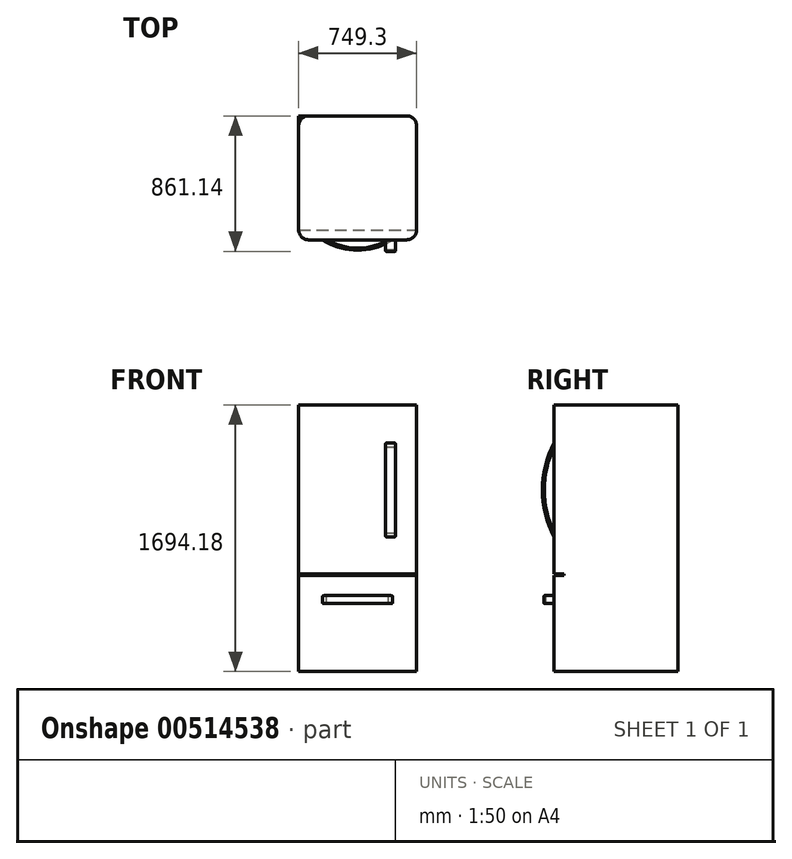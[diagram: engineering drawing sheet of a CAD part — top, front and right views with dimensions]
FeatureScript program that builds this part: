
annotation { "Feature Type Name" : "Feature", "Feature Type Description" : "" }
export const myFeature = defineFeature(function(context is Context, id is Id, definition is map)
    precondition{}
    {
        {
            var Q0;
            Q0=qCreatedBy(makeId("Top.planeOp"),FACE);
            var sketch = newSketch(context, id + "F0", { "sketchPlane" : qUnion([Q0])});
            skLineSegment(sketch, "E0.bottom", {"start": v(374.65, 393.7) * mm, "end": v(-374.65, 393.7) * mm});
            skLineSegment(sketch, "E0.top", {"start": v(374.65, -393.7) * mm, "end": v(-374.65, -393.7) * mm});
            skLineSegment(sketch, "E0.left", {"start": v(374.65, 393.7) * mm, "end": v(374.65, -393.7) * mm});
            skLineSegment(sketch, "E0.right", {"start": v(-374.65, 393.7) * mm, "end": v(-374.65, -393.7) * mm});
            skPoint(sketch, "E0.middle", {"position": v(0, 0) * mm});
            skSolve(sketch);
        }
        {
            var Q0;
            Q0=makeQuery(id+"F0.imprint","IMPRINT",FACE,{"disambiguationData":[TD([[makeQuery(id+"F0.imprint","IMPRINT",EDGE,{"derivedFrom":sQuery(id+"F0.wireOp",EDGE,"E0.bottom")}),1.0]])]});
            extrude(context, id + "F1", {"entities" : qUnion([Q0]), "depth" : 1694.18 * mm, "offsetDistance" : 25.4 * mm});
        }
        {
            var Q0;
            Q0=makeQuery(id+"F1.opExtrude","SWEPT_FACE",FACE,{"disambiguationData":[OSD([sQuery(id+"F0.wireOp",EDGE,"E0.top")])]});
            var sketch = newSketch(context, id + "F2", { "sketchPlane" : qUnion([Q0])});
            skLineSegment(sketch, "E1.bottom", {"start": v(-374.65, 1694.18) * mm, "end": v(374.65, 1694.18) * mm});
            skLineSegment(sketch, "E1.top", {"start": v(-374.65, 619.76) * mm, "end": v(374.65, 619.76) * mm});
            skLineSegment(sketch, "E1.left", {"start": v(-374.65, 1694.18) * mm, "end": v(-374.65, 619.76) * mm});
            skLineSegment(sketch, "E1.right", {"start": v(374.65, 1694.18) * mm, "end": v(374.65, 619.76) * mm});
            skLineSegment(sketch, "E2.bottom", {"start": v(374.65, 0) * mm, "end": v(-374.65, 0) * mm});
            skLineSegment(sketch, "E2.top", {"start": v(374.65, 609.6) * mm, "end": v(-374.65, 609.6) * mm});
            skLineSegment(sketch, "E2.left", {"start": v(374.65, 0) * mm, "end": v(374.65, 609.6) * mm});
            skLineSegment(sketch, "E2.right", {"start": v(-374.65, 0) * mm, "end": v(-374.65, 609.6) * mm});
            skSolve(sketch);
        }
        {
            var Q0;
            {var subQ0=sQuery(id+"F2.wireOp",EDGE,"E1.top");Q0=makeQuery(id+"F2.imprint","IMPRINT",FACE,{"disambiguationData":[TD([[makeQuery(id+"F2.imprint","IMPRINT",EDGE,{"derivedFrom":subQ0}),-1.0]])]});}
            extrude(context, id + "F3", {"entities" : qUnion([Q0]), "operationType" : NewBodyOperationType.REMOVE, "oppositeDirection" : true, "depth" : 63.5 * mm, "offsetDistance" : 25.4 * mm});
        }
        {
            var Q0;
            {var subQ0=sQuery(id+"F0.wireOp",EDGE,"E0.left");var subQ1=sQuery(id+"F0.wireOp",EDGE,"E0.top");Q0=makeQuery(id+"F3.boolean.opBoolean","SPLIT",EDGE,{"disambiguationData":[TD([makeQuery(id+"F3.opExtrude","SWEPT_FACE",FACE,{"disambiguationData":[OSD([sQuery(id+"F2.wireOp",EDGE,"E1.top")])]})])],"derivedFrom":makeQuery(id+"F1.opExtrude","SWEPT_EDGE",EDGE,{"disambiguationData":[OSD([subQ1,subQ0])]})});}
            var Q1;
            {var subQ0=sQuery(id+"F0.wireOp",EDGE,"E0.left");var subQ1=sQuery(id+"F0.wireOp",EDGE,"E0.top");Q1=makeQuery(id+"F3.boolean.opBoolean","SPLIT",EDGE,{"disambiguationData":[TD([makeQuery(id+"F3.opExtrude","SWEPT_FACE",FACE,{"disambiguationData":[OSD([sQuery(id+"F2.wireOp",EDGE,"E2.top")])]})])],"derivedFrom":makeQuery(id+"F1.opExtrude","SWEPT_EDGE",EDGE,{"disambiguationData":[OSD([subQ1,subQ0])]})});}
            var Q2;
            {var subQ0=sQuery(id+"F0.wireOp",EDGE,"E0.right");var subQ1=sQuery(id+"F0.wireOp",EDGE,"E0.top");Q2=makeQuery(id+"F3.boolean.opBoolean","SPLIT",EDGE,{"disambiguationData":[TD([makeQuery(id+"F3.opExtrude","SWEPT_FACE",FACE,{"disambiguationData":[OSD([sQuery(id+"F2.wireOp",EDGE,"E1.top")])]})])],"derivedFrom":makeQuery(id+"F1.opExtrude","SWEPT_EDGE",EDGE,{"disambiguationData":[OSD([subQ1,subQ0])]})});}
            var Q3;
            {var subQ0=sQuery(id+"F0.wireOp",EDGE,"E0.right");var subQ1=sQuery(id+"F0.wireOp",EDGE,"E0.top");Q3=makeQuery(id+"F3.boolean.opBoolean","SPLIT",EDGE,{"disambiguationData":[TD([makeQuery(id+"F3.opExtrude","SWEPT_FACE",FACE,{"disambiguationData":[OSD([sQuery(id+"F2.wireOp",EDGE,"E2.top")])]})])],"derivedFrom":makeQuery(id+"F1.opExtrude","SWEPT_EDGE",EDGE,{"disambiguationData":[OSD([subQ1,subQ0])]})});}
            var Q4;
            Q4=makeQuery(id+"F1.opExtrude","SWEPT_EDGE",EDGE,{"disambiguationData":[OSD([sQuery(id+"F0.wireOp",EDGE,"E0.bottom"),sQuery(id+"F0.wireOp",EDGE,"E0.left")])]});
            var Q5;
            Q5=makeQuery(id+"F1.opExtrude","SWEPT_EDGE",EDGE,{"disambiguationData":[OSD([sQuery(id+"F0.wireOp",EDGE,"E0.bottom"),sQuery(id+"F0.wireOp",EDGE,"E0.right")])]});
            fillet(context, id + "F4", {"entities" : qUnion([Q0, Q1, Q2, Q3, Q4, Q5]), "radius" : 63.5 * mm, "tangentPropagation" : true, "allowEdgeOverflow" : false});
        }
        {
            var Q0;
            Q0=makeQuery(id+"F1.opExtrude","CAP_FACE",FACE,{"disambiguationData":[OSD([sQuery(id+"F0.wireOp",EDGE,"E0.bottom"),sQuery(id+"F0.wireOp",EDGE,"E0.top"),sQuery(id+"F0.wireOp",EDGE,"E0.left"),sQuery(id+"F0.wireOp",EDGE,"E0.right")])],"isStart":true});
            cPlane(context, id + "F5", {"entities" : qUnion([Q0]), "cplaneType" : CPlaneType.OFFSET, "offset" : 457.2 * mm, "oppositeDirection" : true, "width" : 152.4 * mm, "height" : 152.4 * mm});
        }
        {
            var Q0;
            Q0=qCreatedBy(id+"F5.planeOp",FACE);
            var sketch = newSketch(context, id + "F6", { "sketchPlane" : qUnion([Q0])});
            skLineSegment(sketch, "E3", {"start": v(-311.15, 477.49) * mm, "end": v(-209.55, 477.49) * mm});
            skLineSegment(sketch, "E4", {"start": v(-209.55, 477.49) * mm, "end": v(209.55, 477.49) * mm});
            skLineSegment(sketch, "E5", {"start": v(209.55, 477.49) * mm, "end": v(311.15, 477.49) * mm});
            skLineSegment(sketch, "E6", {"start": v(0, 0) * mm, "end": v(0, 4953.26) * mm});
            skLineSegment(sketch, "E7", {"start": v(-209.55, 477.49) * mm, "end": v(0, 477.49) * mm});
            skCircle(sketch, "E8", {"center": v(0, 50.8) * mm, "radius": 254 * mm});
            skArc(sketch, "E9", {"start": v(209.67, 194.17) * mm, "mid": v(5.68, 304.74) * mm, "end": v(-203.05, 203.4) * mm});
            skSolve(sketch);
        }
        {
            var Q0;
            Q0=makeQuery(id+"F2.imprint","IMPRINT",FACE,{"disambiguationData":[TD([[makeQuery(id+"F2.imprint","IMPRINT",EDGE,{"derivedFrom":sQuery(id+"F2.wireOp",EDGE,"E2.bottom")}),-1.0]])]});
            var sketch = newSketch(context, id + "F7", { "sketchPlane" : qUnion([Q0])});
            skLineSegment(sketch, "E10", {"start": v(-209.55, 609.6) * mm, "end": v(-209.55, 457.2) * mm});
            skLineSegment(sketch, "E11", {"start": v(-311.15, 457.2) * mm, "end": v(-209.55, 457.2) * mm});
            skLineSegment(sketch, "E12", {"start": v(-209.55, 457.2) * mm, "end": v(209.55, 457.2) * mm});
            skLineSegment(sketch, "E13", {"start": v(209.55, 457.2) * mm, "end": v(311.15, 457.2) * mm});
            skLineSegment(sketch, "E14.bottom", {"start": v(-196.85, 482.6) * mm, "end": v(-222.25, 482.6) * mm});
            skLineSegment(sketch, "E14.top", {"start": v(-196.85, 431.8) * mm, "end": v(-222.25, 431.8) * mm});
            skLineSegment(sketch, "E14.left", {"start": v(-196.85, 482.6) * mm, "end": v(-196.85, 431.8) * mm});
            skLineSegment(sketch, "E14.right", {"start": v(-222.25, 482.6) * mm, "end": v(-222.25, 431.8) * mm});
            skPoint(sketch, "E14.middle", {"position": v(-209.55, 457.2) * mm});
            skSolve(sketch);
        }
        {
            var Q0;
            Q0 = qSketchRegion(id + "F7", true);
            var Q1;
            Q1=sQuery(id+"F6.wireOp",EDGE,"E9");
            sweep(context, id + "F8", {"operationType" : NewBodyOperationType.ADD, "profiles" : qUnion([Q0]), "path" : qUnion([Q1])});
        }
        {
            var Q0;
            Q0=makeQuery(id+"F8.opSweep","SWEPT_EDGE",EDGE,{"disambiguationData":[OSD([sQuery(id+"F6.wireOp",EDGE,"E9"),sQuery(id+"F7.wireOp",EDGE,"E14.bottom"),sQuery(id+"F7.wireOp",EDGE,"E14.right")])]});
            var Q1;
            Q1=makeQuery(id+"F8.opSweep","SWEPT_EDGE",EDGE,{"disambiguationData":[OSD([sQuery(id+"F6.wireOp",EDGE,"E9"),sQuery(id+"F7.wireOp",EDGE,"E14.bottom"),sQuery(id+"F7.wireOp",EDGE,"E14.left")])]});
            var Q2;
            Q2=makeQuery(id+"F8.opSweep","SWEPT_EDGE",EDGE,{"disambiguationData":[OSD([sQuery(id+"F6.wireOp",EDGE,"E9"),sQuery(id+"F7.wireOp",EDGE,"E14.top"),sQuery(id+"F7.wireOp",EDGE,"E14.right")])]});
            var Q3;
            Q3=makeQuery(id+"F8.opSweep","SWEPT_EDGE",EDGE,{"disambiguationData":[OSD([sQuery(id+"F6.wireOp",EDGE,"E9"),sQuery(id+"F7.wireOp",EDGE,"E14.top"),sQuery(id+"F7.wireOp",EDGE,"E14.left")])]});
            fillet(context, id + "F9", {"entities" : qUnion([Q0, Q1, Q2, Q3]), "radius" : 5.08 * mm, "tangentPropagation" : true, "allowEdgeOverflow" : false});
        }
        {
            var Q0;
            Q0=makeQuery(id+"F2.imprint","IMPRINT",FACE,{"disambiguationData":[TD([[makeQuery(id+"F2.imprint","IMPRINT",EDGE,{"derivedFrom":sQuery(id+"F2.wireOp",EDGE,"E1.bottom")}),1.0]])]});
            var sketch = newSketch(context, id + "F10", { "sketchPlane" : qUnion([Q0])});
            skLineSegment(sketch, "E15", {"start": v(209.55, 1694.18) * mm, "end": v(209.55, 619.76) * mm});
            skLineSegment(sketch, "E16", {"start": v(209.55, 619.76) * mm, "end": v(209.55, 873.76) * mm});
            skLineSegment(sketch, "E17", {"start": v(209.55, 873.76) * mm, "end": v(209.55, 1440.18) * mm});
            skLineSegment(sketch, "E18", {"start": v(209.55, 1440.18) * mm, "end": v(209.55, 1694.18) * mm});
            skLineSegment(sketch, "E19.bottom", {"start": v(241.3, 1452.88) * mm, "end": v(177.8, 1452.88) * mm});
            skLineSegment(sketch, "E19.top", {"start": v(241.3, 1427.48) * mm, "end": v(177.8, 1427.48) * mm});
            skLineSegment(sketch, "E19.left", {"start": v(241.3, 1452.88) * mm, "end": v(241.3, 1427.48) * mm});
            skLineSegment(sketch, "E19.right", {"start": v(177.8, 1452.88) * mm, "end": v(177.8, 1427.48) * mm});
            skPoint(sketch, "E19.middle", {"position": v(209.55, 1440.18) * mm});
            skSolve(sketch);
        }
        {
            var Q0;
            Q0=makeQuery(id+"F1.opExtrude","SWEPT_FACE",FACE,{"disambiguationData":[OSD([sQuery(id+"F0.wireOp",EDGE,"E0.left")])]});
            cPlane(context, id + "F11", {"entities" : qUnion([Q0]), "cplaneType" : CPlaneType.OFFSET, "offset" : 165.1 * mm, "oppositeDirection" : true, "width" : 152.4 * mm, "height" : 152.4 * mm});
        }
        {
            var Q0;
            Q0=qCreatedBy(id+"F11.planeOp",FACE);
            var sketch = newSketch(context, id + "F12", { "sketchPlane" : qUnion([Q0])});
            skLineSegment(sketch, "E20", {"start": v(-393.7, 1440.18) * mm, "end": v(-393.7, 868.68) * mm});
            skArc(sketch, "E21", {"start": v(-393.7, 1440.18) * mm, "mid": v(-461.63, 1154.43) * mm, "end": v(-393.7, 868.68) * mm});
            skArc(sketch, "E22", {"start": v(-280.48, 1598.55) * mm, "mid": v(-461.63, 1154.43) * mm, "end": v(-280.48, 710.3) * mm});
            skLineSegment(sketch, "E23", {"start": v(-280.48, 1598.55) * mm, "end": v(-280.48, 710.3) * mm});
            skSolve(sketch);
        }
        {
            var Q0;
            Q0 = qSketchRegion(id + "F10", true);
            var Q1;
            Q1=sQuery(id+"F12.wireOp",EDGE,"E22");
            sweep(context, id + "F13", {"operationType" : NewBodyOperationType.ADD, "profiles" : qUnion([Q0]), "path" : qUnion([Q1])});
        }
        {
            var Q0;
            Q0=makeQuery(id+"F13.opSweep","SWEPT_EDGE",EDGE,{"disambiguationData":[OSD([sQuery(id+"F10.wireOp",EDGE,"E19.top"),sQuery(id+"F10.wireOp",EDGE,"E19.left"),sQuery(id+"F12.wireOp",EDGE,"E22")])]});
            var Q1;
            Q1=makeQuery(id+"F13.opSweep","SWEPT_EDGE",EDGE,{"disambiguationData":[OSD([sQuery(id+"F10.wireOp",EDGE,"E19.bottom"),sQuery(id+"F10.wireOp",EDGE,"E19.left"),sQuery(id+"F12.wireOp",EDGE,"E22")])]});
            var Q2;
            Q2=makeQuery(id+"F13.opSweep","SWEPT_EDGE",EDGE,{"disambiguationData":[OSD([sQuery(id+"F10.wireOp",EDGE,"E19.bottom"),sQuery(id+"F10.wireOp",EDGE,"E19.right"),sQuery(id+"F12.wireOp",EDGE,"E22")])]});
            var Q3;
            Q3=makeQuery(id+"F13.opSweep","SWEPT_EDGE",EDGE,{"disambiguationData":[OSD([sQuery(id+"F10.wireOp",EDGE,"E19.top"),sQuery(id+"F10.wireOp",EDGE,"E19.right"),sQuery(id+"F12.wireOp",EDGE,"E22")])]});
            fillet(context, id + "F14", {"entities" : qUnion([Q0, Q1, Q2, Q3]), "radius" : 5.08 * mm, "tangentPropagation" : true, "allowEdgeOverflow" : false});
        }
        {
            var Q0;
            Q0=makeQuery(id+"F1.opExtrude","CAP_FACE",FACE,{"disambiguationData":[OSD([sQuery(id+"F0.wireOp",EDGE,"E0.bottom"),sQuery(id+"F0.wireOp",EDGE,"E0.top"),sQuery(id+"F0.wireOp",EDGE,"E0.left"),sQuery(id+"F0.wireOp",EDGE,"E0.right")])],"isStart":true});
            var sketch = newSketch(context, id + "F15", { "sketchPlane" : qUnion([Q0])});
            skLineSegment(sketch, "E24.bottom", {"start": v(-374.65, -330.2) * mm, "end": v(-311.15, -330.2) * mm});
            skLineSegment(sketch, "E24.top", {"start": v(-374.65, -393.7) * mm, "end": v(-311.15, -393.7) * mm});
            skLineSegment(sketch, "E24.left", {"start": v(-374.65, -330.2) * mm, "end": v(-374.65, -393.7) * mm});
            skLineSegment(sketch, "E24.right", {"start": v(-311.15, -330.2) * mm, "end": v(-311.15, -393.7) * mm});
            skSolve(sketch);
        }
        {
            var Q0;
            Q0=makeQuery(id+"F15.imprint","IMPRINT",FACE,{"disambiguationData":[TD([[makeQuery(id+"F15.imprint","IMPRINT",EDGE,{"derivedFrom":sQuery(id+"F15.wireOp",EDGE,"E24.top")}),1.0]])]});
            extrude(context, id + "F16", {"entities" : qUnion([Q0]), "operationType" : NewBodyOperationType.ADD, "oppositeDirection" : true, "depth" : 2.54 * mm, "offsetDistance" : 25.4 * mm});
        }
    });
